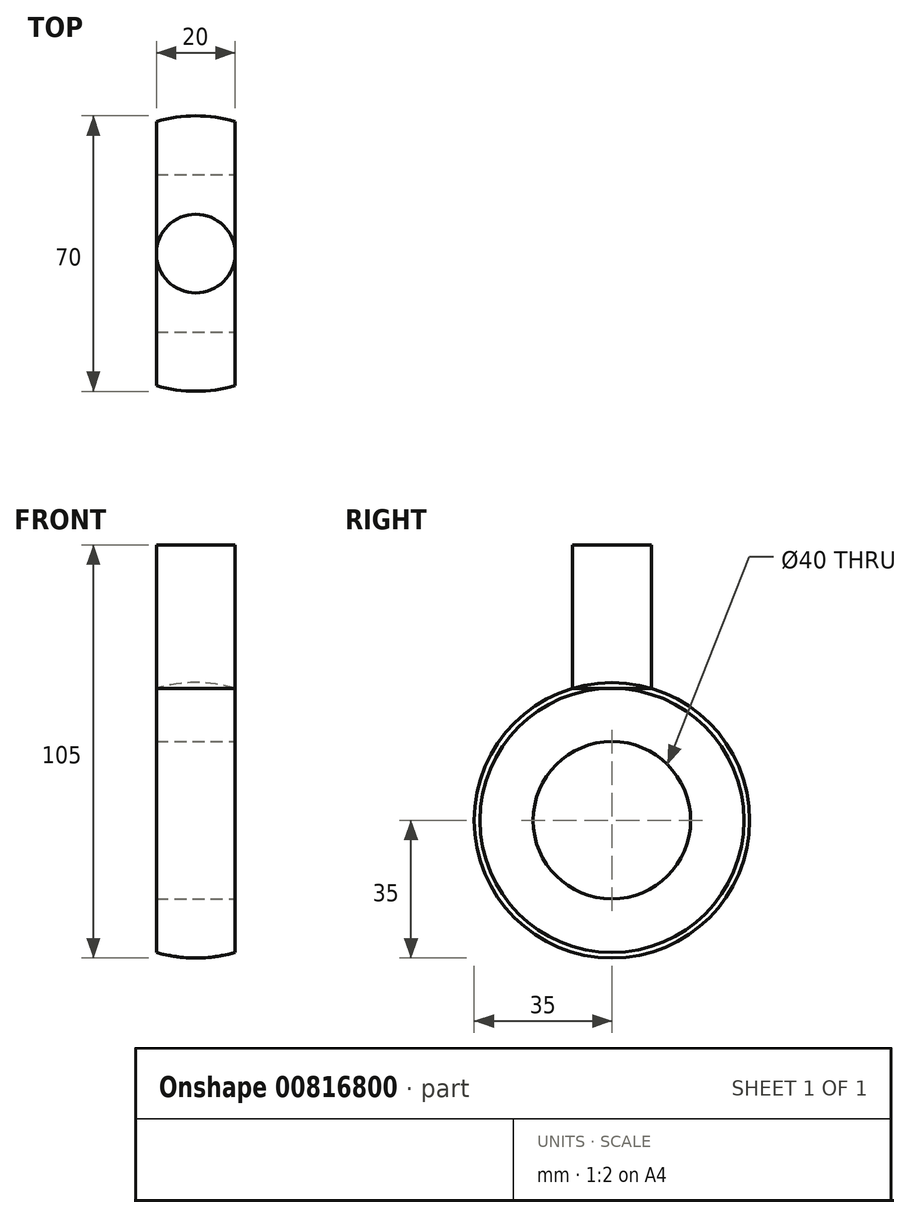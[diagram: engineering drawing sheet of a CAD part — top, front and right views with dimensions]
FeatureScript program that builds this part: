
annotation { "Feature Type Name" : "Feature", "Feature Type Description" : "" }
export const myFeature = defineFeature(function(context is Context, id is Id, definition is map)
    precondition{}
    {
        {
            var Q0;
            Q0=qCreatedBy(makeId("Top.planeOp"),FACE);
            var sketch = newSketch(context, id + "F0", { "sketchPlane" : qUnion([Q0])});
            skArc(sketch, "E0", {"start": v(0, 35) * mm, "mid": v(-5.05, 34.63) * mm, "end": v(-10, 33.54) * mm});
            skLineSegment(sketch, "E1", {"start": v(0, 0) * mm, "end": v(-10, 0) * mm});
            skLineSegment(sketch, "E2", {"start": v(-10, 33.54) * mm, "end": v(-10, 0) * mm});
            skLineSegment(sketch, "E3", {"start": v(0, 0) * mm, "end": v(0, 20) * mm});
            skLineSegment(sketch, "E4", {"start": v(0, 20) * mm, "end": v(-10, 20) * mm});
            skLineSegment(sketch, "E5", {"start": v(-10, 20) * mm, "end": v(0, 20) * mm});
            skLineSegment(sketch, "E6", {"start": v(0, 20) * mm, "end": v(0, 35) * mm});
            skArc(sketch, "E7.MirrorCS", {"start": v(0, 35) * mm, "mid": v(5.05, 34.63) * mm, "end": v(10, 33.54) * mm});
            skLineSegment(sketch, "E8.MirrorCS", {"start": v(10, 33.54) * mm, "end": v(10, 0) * mm});
            skLineSegment(sketch, "E9.MirrorCS", {"start": v(10, 20) * mm, "end": v(0, 20) * mm});
            skSolve(sketch);
        }
        {
            var Q0;
            Q0=makeQuery(id+"F0.imprint","IMPRINT",FACE,{"disambiguationData":[TD([[makeQuery(id+"F0.imprint","IMPRINT",EDGE,{"derivedFrom":sQuery(id+"F0.wireOp",EDGE,"E6")}),-1.0]])]});
            var Q1;
            {var subQ0=sQuery(id+"F0.wireOp",EDGE,"E0");Q1=makeQuery(id+"F0.imprint","IMPRINT",FACE,{"disambiguationData":[TD([[makeQuery(id+"F0.imprint","IMPRINT",EDGE,{"derivedFrom":subQ0}),1.0]])]});}
            var Q2;
            Q2=sQuery(id+"F0.wireOp",EDGE,"E1");
            revolve(context, id + "F1", {"surfaceOperationType" : NewSurfaceOperationType.NEW, "entities" : qUnion([Q0, Q1]), "axis" : qUnion([Q2]), "revolveType" : RevolveType.FULL});
        }
        {
            var Q0;
            Q0=qCreatedBy(makeId("Top.planeOp"),FACE);
            cPlane(context, id + "F2", {"entities" : qUnion([Q0]), "cplaneType" : CPlaneType.OFFSET, "offset" : 70 * mm, "width" : 150 * mm, "height" : 150 * mm});
        }
        {
            var Q0;
            Q0=qCreatedBy(id+"F2.planeOp",FACE);
            var sketch = newSketch(context, id + "F3", { "sketchPlane" : qUnion([Q0])});
            skCircle(sketch, "E10", {"center": v(0, 0) * mm, "radius": 10 * mm});
            skSolve(sketch);
        }
        {
            var Q0;
            Q0=makeQuery(id+"F3.imprint","IMPRINT",FACE,{"disambiguationData":[TD([[makeQuery(id+"F3.imprint","IMPRINT",EDGE,{"derivedFrom":sQuery(id+"F3.wireOp",EDGE,"E10")}),1.0]])]});
            extrude(context, id + "F4", {"entities" : qUnion([Q0]), "endBound" : BoundingType.UP_TO_NEXT, "oppositeDirection" : true, "depth" : 25 * mm, "offsetDistance" : 25 * mm});
        }
    });
